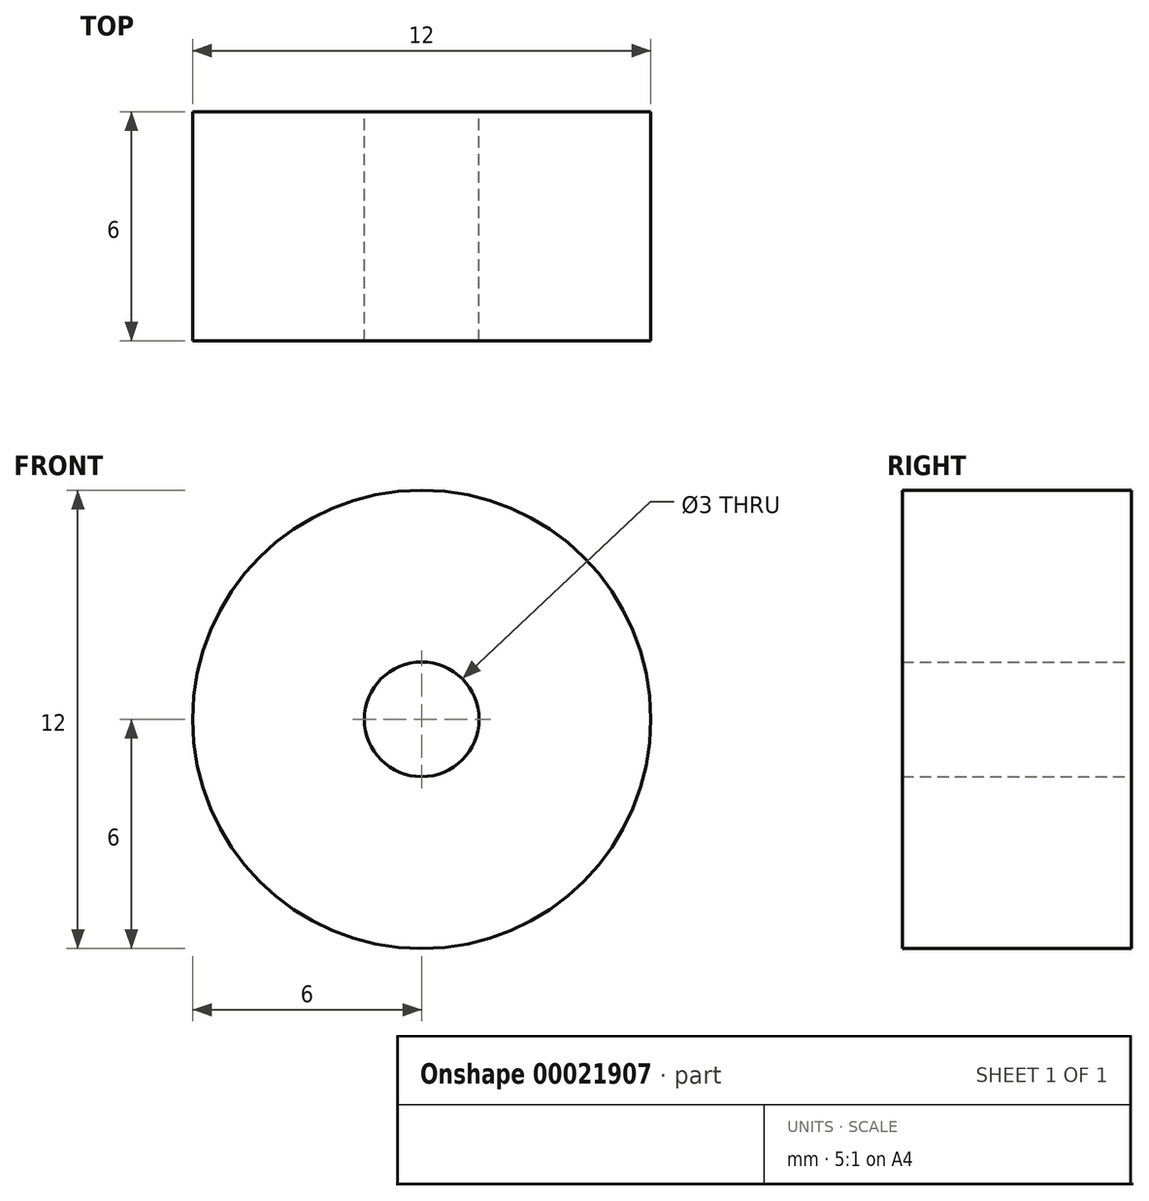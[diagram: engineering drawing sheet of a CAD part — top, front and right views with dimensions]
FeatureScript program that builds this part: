
annotation { "Feature Type Name" : "Feature", "Feature Type Description" : "" }
export const myFeature = defineFeature(function(context is Context, id is Id, definition is map)
    precondition{}
    {
        {
            var Q0;
            Q0=qCreatedBy(makeId("Front.planeOp"),FACE);
            var sketch = newSketch(context, id + "F0", { "sketchPlane" : qUnion([Q0])});
            skCircle(sketch, "E0", {"center": v(0, 0) * mm, "radius": 6 * mm});
            skCircle(sketch, "E1", {"center": v(0, 0) * mm, "radius": 1.5 * mm});
            skSolve(sketch);
        }
        {
            var Q0;
            Q0=qSketchRegion(id+"F0",true);
            var Q1;
            Q1=makeQuery(id+"F0.imprint","IMPRINT",FACE,{"disambiguationData":[TD([[makeQuery(id+"F0.imprint","IMPRINT",EDGE,{"derivedFrom":sQuery(id+"F0.wireOp",EDGE,"6ba5e74c-d761-4b98-a911-20bb2d00977a")}),1.0]])]});
            extrude(context, id + "F1", {"entities" : qUnion([Q0, Q1]), "depth" : 6 * mm});
        }
    });
